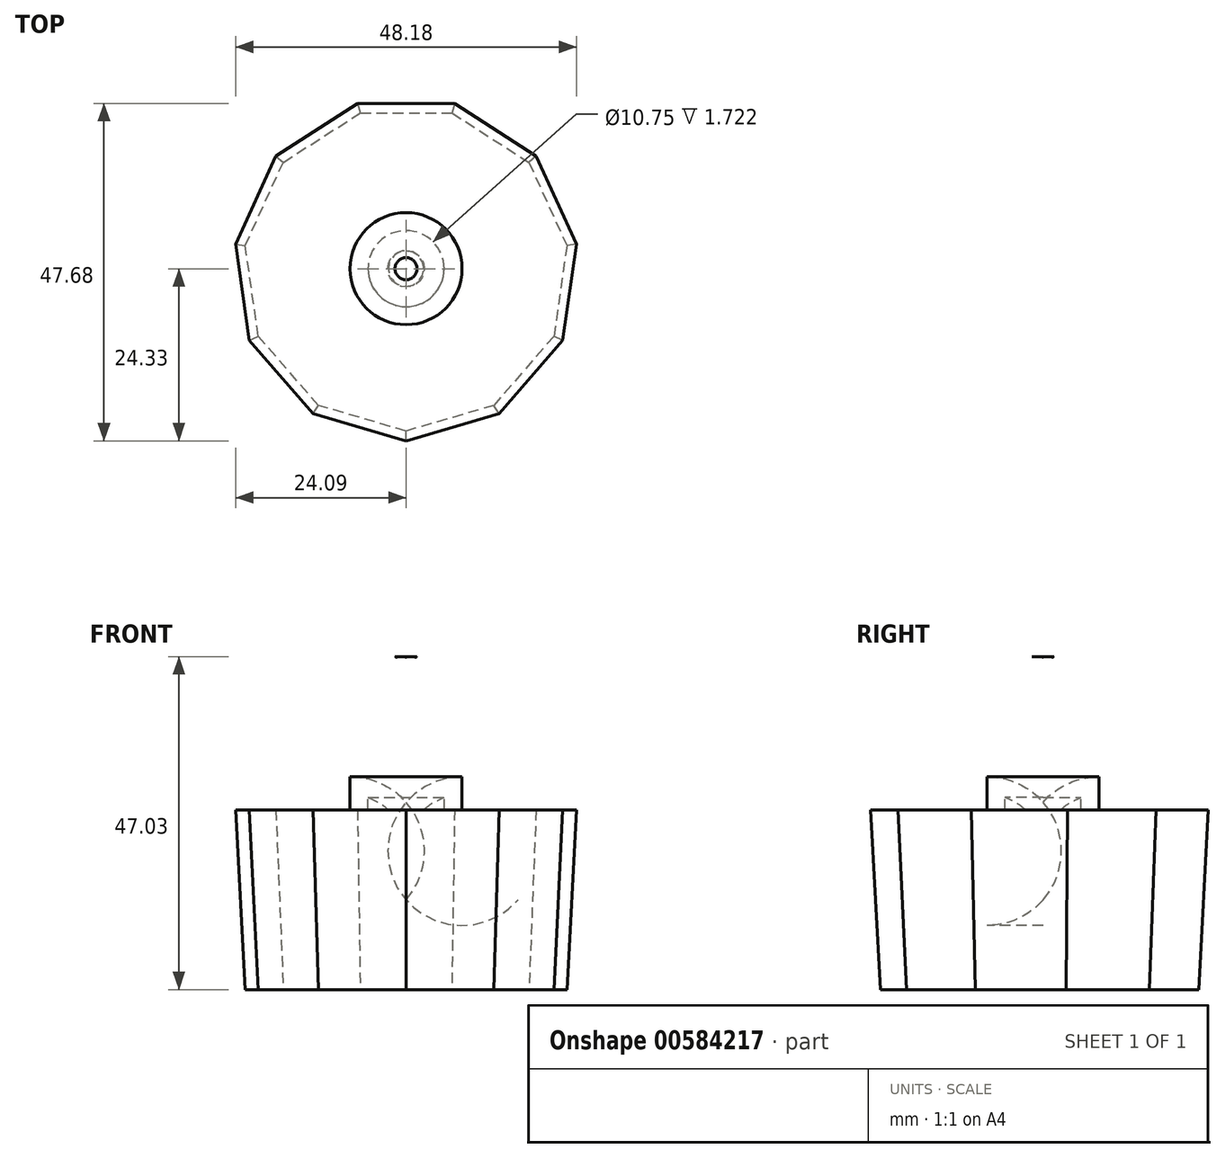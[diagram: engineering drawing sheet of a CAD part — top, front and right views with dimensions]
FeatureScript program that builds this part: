
annotation { "Feature Type Name" : "Feature", "Feature Type Description" : "" }
export const myFeature = defineFeature(function(context is Context, id is Id, definition is map)
    precondition{}
    {
        {
            var Q0;
            Q0=qCreatedBy(makeId("Front.planeOp"),FACE);
            var sketch = newSketch(context, id + "F0", { "sketchPlane" : qUnion([Q0])});
            skLineSegment(sketch, "E0", {"start": v(0, 42.45) * mm, "end": v(0, 0) * mm});
            skArc(sketch, "E1", {"start": v(0, 0) * mm, "mid": v(21.85, 21.23) * mm, "end": v(0, 42.45) * mm});
            skSolve(sketch);
        }
        {
            var Q0;
            Q0=makeQuery(id+"F0.imprint","IMPRINT",FACE,{"disambiguationData":[TD([[makeQuery(id+"F0.imprint","IMPRINT",EDGE,{"derivedFrom":sQuery(id+"F0.wireOp",EDGE,"E0")}),1.0]])]});
            var Q1;
            Q1=sQuery(id+"F0.wireOp",EDGE,"E0");
            revolve(context, id + "F1", {"entities" : qUnion([Q0]), "axis" : qUnion([Q1]), "revolveType" : RevolveType.FULL});
        }
        {
            var Q0;
            Q0=qCreatedBy(makeId("Front.planeOp"),FACE);
            var sketch = newSketch(context, id + "F2", { "sketchPlane" : qUnion([Q0])});
            skLineSegment(sketch, "E2", {"start": v(0, 0) * mm, "end": v(0, -39) * mm});
            skArc(sketch, "E3", {"start": v(0, -19.5) * mm, "mid": v(10.64, -9.75) * mm, "end": v(0, 0) * mm});
            skArc(sketch, "E4", {"start": v(7.91, -31.23) * mm, "mid": v(10.27, -34.8) * mm, "end": v(11.1, -39) * mm});
            skArc(sketch, "E5", {"start": v(0, -24.32) * mm, "mid": v(3.57, -21.66) * mm, "end": v(7.91, -20.72) * mm});
            skLineSegment(sketch, "E6", {"start": v(7.91, -20.72) * mm, "end": v(7.91, -31.23) * mm});
            skLineSegment(sketch, "E7", {"start": v(0, -39) * mm, "end": v(11.1, -39) * mm});
            skSolve(sketch);
        }
        {
            var Q0;
            Q0 = qSketchRegion(id + "F2", true);
            var Q1;
            Q1=sQuery(id+"F2.wireOp",EDGE,"E2");
            revolve(context, id + "F3", {"operationType" : NewBodyOperationType.ADD, "entities" : qUnion([Q0]), "axis" : qUnion([Q1]), "revolveType" : RevolveType.FULL});
        }
        {
            var Q0;
            Q0=makeQuery(id+"F3.opRevolve","SWEPT_FACE",FACE,{"disambiguationData":[OSD([sQuery(id+"F2.wireOp",EDGE,"E7")])]});
            shell(context, id + "F4", {"entities" : qUnion([Q0]), "thickness" : 2.54 * mm});
        }
        {
            var Q0;
            Q0=makeQuery(id+"F4.opShell","OFFSET_EDGE",EDGE,{"disambiguationData":[OSD([sQuery(id+"F2.wireOp",EDGE,"E4"),sQuery(id+"F2.wireOp",EDGE,"E7")])]});
            fillet(context, id + "F5", {"entities" : qUnion([Q0]), "radius" : 40.47 * mm, "tangentPropagation" : true, "allowEdgeOverflow" : false});
        }
        {
            var Q0;
            Q0=qCreatedBy(makeId("Top.planeOp"),FACE);
            cPlane(context, id + "F6", {"entities" : qUnion([Q0]), "cplaneType" : CPlaneType.OFFSET, "offset" : 50.8 * mm, "oppositeDirection" : true, "width" : 152.4 * mm, "height" : 152.4 * mm});
        }
        {
            var Q0;
            Q0=qCreatedBy(id+"F6.planeOp",FACE);
            var sketch = newSketch(context, id + "F7", { "sketchPlane" : qUnion([Q0])});
            skCircle(sketch, "E8.cCircle", {"center": v(0, 0) * mm, "radius": 22.02 * mm, "construction": true});
            skLineSegment(sketch, "E8.0", {"start": v(-6.46, 22.02) * mm, "end": v(6.46, 22.02) * mm});
            skLineSegment(sketch, "E8.1", {"start": v(6.46, 22.02) * mm, "end": v(17.34, 15.03) * mm});
            skLineSegment(sketch, "E8.2", {"start": v(17.34, 15.03) * mm, "end": v(22.71, 3.27) * mm});
            skLineSegment(sketch, "E8.3", {"start": v(22.71, 3.27) * mm, "end": v(20.87, -9.53) * mm});
            skLineSegment(sketch, "E8.4", {"start": v(20.87, -9.53) * mm, "end": v(12.4, -19.3) * mm});
            skLineSegment(sketch, "E8.5", {"start": v(12.4, -19.3) * mm, "end": v(0, -22.95) * mm});
            skLineSegment(sketch, "E8.6", {"start": v(0, -22.95) * mm, "end": v(-12.4, -19.3) * mm});
            skLineSegment(sketch, "E8.7", {"start": v(-12.4, -19.3) * mm, "end": v(-20.87, -9.53) * mm});
            skLineSegment(sketch, "E8.8", {"start": v(-20.87, -9.53) * mm, "end": v(-22.71, 3.27) * mm});
            skLineSegment(sketch, "E8.9", {"start": v(-22.71, 3.27) * mm, "end": v(-17.34, 15.03) * mm});
            skLineSegment(sketch, "E8.10", {"start": v(-17.34, 15.03) * mm, "end": v(-6.46, 22.02) * mm});
            skPoint(sketch, "E8.0.midPoint", {"position": v(0, 22.02) * mm});
            skSolve(sketch);
        }
        {
            var Q0;
            Q0=makeQuery(id+"F7.imprint","IMPRINT",FACE,{"disambiguationData":[TD([[makeQuery(id+"F7.imprint","IMPRINT",EDGE,{"derivedFrom":sQuery(id+"F7.wireOp",EDGE,"E8.0")}),-1.0]])]});
            extrude(context, id + "F8", {"entities" : qUnion([Q0]), "operationType" : NewBodyOperationType.ADD, "depth" : 25.4 * mm, "offsetDistance" : 25.4 * mm, "hasDraft" : true, "draftAngle" : 3 * degree});
        }
        {
            var Q0;
            Q0=makeQuery(id+"F3.opRevolve","SWEPT_BODY",BODY,{"disambiguationData":[OSD([sQuery(id+"F2.wireOp",EDGE,"E2"),sQuery(id+"F2.wireOp",EDGE,"E4"),sQuery(id+"F2.wireOp",EDGE,"E5"),sQuery(id+"F2.wireOp",EDGE,"E6"),sQuery(id+"F2.wireOp",EDGE,"E7")])]});
            transform(context, id + "F9", {"entities" : qUnion([Q0]), "transformType" : TransformType.TRANSLATION_3D, "dx" : 0 * mm, "dy" : 0 * mm, "dz" : 3.81 * mm, "makeCopy" : false});
        }
    });
